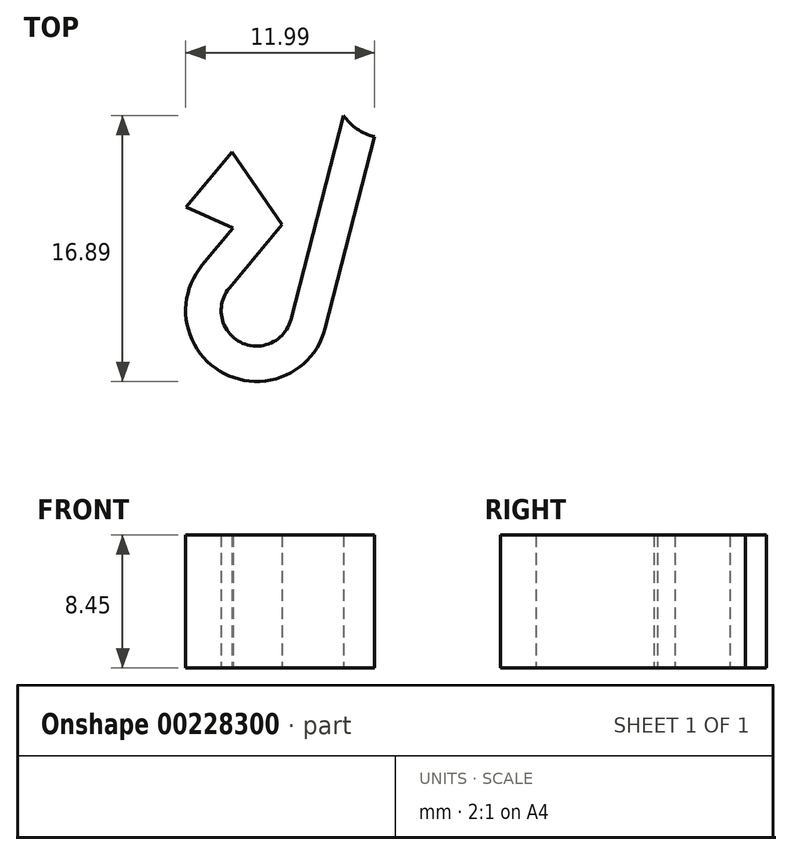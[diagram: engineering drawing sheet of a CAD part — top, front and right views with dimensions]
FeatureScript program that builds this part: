
annotation { "Feature Type Name" : "Feature", "Feature Type Description" : "" }
export const myFeature = defineFeature(function(context is Context, id is Id, definition is map)
    precondition{}
    {
        {
            var Q0;
            Q0=qCreatedBy(makeId("Top.planeOp"),FACE);
            var sketch = newSketch(context, id + "F0", { "sketchPlane" : qUnion([Q0])});
            skLineSegment(sketch, "E0", {"start": v(23.6, 25.66) * mm, "end": v(23.6, -15.81) * mm, "construction": true});
            skLineSegment(sketch, "E1", {"start": v(-23.6, 23.16) * mm, "end": v(-23.6, -15.12) * mm, "construction": true});
            skCircle(sketch, "E2", {"center": v(0, 0) * mm, "radius": 3.3 * mm});
            skLineSegment(sketch, "E3", {"start": v(-3.1, -1.12) * mm, "end": v(-14.99, -15.34) * mm});
            skCircle(sketch, "E4", {"center": v(0, 0) * mm, "radius": 21.45 * mm, "construction": true});
            skLineSegment(sketch, "E5", {"start": v(0, 29.8) * mm, "end": v(0, -28.76) * mm, "construction": true});
            skLineSegment(sketch, "E6", {"start": v(-8, -6.98) * mm, "end": v(-9.92, -4.2) * mm});
            skLineSegment(sketch, "E7", {"start": v(-9.92, -4.2) * mm, "end": v(-13, -7.88) * mm});
            skLineSegment(sketch, "E8", {"start": v(-13, -7.88) * mm, "end": v(-9.92, -9.28) * mm});
            skLineSegment(sketch, "E9", {"start": v(-3.1, -1.12) * mm, "end": v(8.3, 12.53) * mm, "construction": true});
            skPoint(sketch, "E10", {"position": v(0.55, 3.25) * mm});
            skPoint(sketch, "E11", {"position": v(-8.96, -8.13) * mm});
            skLineSegment(sketch, "E12", {"start": v(-8.96, -8.13) * mm, "end": v(-15.07, -3.02) * mm, "construction": true});
            skLineSegment(sketch, "E13", {"start": v(0, 0) * mm, "end": v(-5.35, -20.77) * mm});
            skArc(sketch, "E14", {"start": v(-11.82, -11.55) * mm, "mid": v(-10.42, -18.44) * mm, "end": v(-4, -15.56) * mm});
            skCircle(sketch, "E15", {"center": v(-8.36, -14.43) * mm, "radius": 2.25 * mm});
            skLineSegment(sketch, "E16", {"start": v(-6.18, -15) * mm, "end": v(-2.78, -1.78) * mm});
            skLineSegment(sketch, "E17", {"start": v(-8, -6.98) * mm, "end": v(-6.67, -8.9) * mm});
            skLineSegment(sketch, "E18", {"start": v(-10.1, -13) * mm, "end": v(-6.67, -8.9) * mm});
            skLineSegment(sketch, "E19.0", {"start": v(-12.84, -7.85) * mm, "end": v(-9.86, -9.2) * mm});
            skLineSegment(sketch, "E19.1", {"start": v(-9.93, -4.36) * mm, "end": v(-12.84, -7.85) * mm});
            skLineSegment(sketch, "E19.2", {"start": v(-8.08, -7.03) * mm, "end": v(-9.93, -4.36) * mm});
            skLineSegment(sketch, "E19.3", {"start": v(-8.08, -7.03) * mm, "end": v(-6.74, -8.98) * mm});
            skCircle(sketch, "E20", {"center": v(0, 0) * mm, "radius": 3.5 * mm});
            skSolve(sketch);
        }
        {
            var Q0;
            {var subQ0=sQuery(id+"F0.wireOp",EDGE,"E14");Q0=makeQuery(id+"F0.imprint","IMPRINT",FACE,{"disambiguationData":[TD([[makeQuery(id+"F0.imprint","IMPRINT",EDGE,{"derivedFrom":subQ0}),1.0]])]});}
            var Q1;
            {var subQ1=sQuery(id+"F0.wireOp",EDGE,"E19.0");Q1=makeQuery(id+"F0.imprint","IMPRINT",FACE,{"disambiguationData":[TD([[makeQuery(id+"F0.imprint","IMPRINT",EDGE,{"derivedFrom":subQ1}),1.0]])]});}
            extrude(context, id + "F1", {"entities" : qUnion([Q0, Q1]), "depth" : 8.45 * mm});
        }
    });
